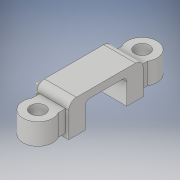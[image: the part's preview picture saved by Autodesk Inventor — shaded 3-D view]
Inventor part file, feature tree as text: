
AUTODESK INVENTOR PART (.ipt)
format: ipt  version: 2018 (Build 220112000, 112)  size: 198,144 bytes
history: native  units: in
note: dims shown in document units (in); Inventor stores cm internally (conversion verified against a paired STEP export)
features: sketch x10, extrude x6, fillet x2
ambient origin geometry x8: Origin, YZ Plane, XZ Plane, XY Plane, X Axis, Y Axis, Z Axis, Center Point
bodies: Solid1 (feature_tree)
feature tree (18):
  sketch  "Sketch1"  dims[d0=1.378in d1=0.5906in]
  sketch  "Sketch2"  dims[d2=0.1378in d3=0.0in d4=0.2559in d5=0.2559in]
  extrude  "Extrusion1"  Depth=0.5906in
  sketch  "Sketch4"  dims[d14=0.5512in d15=0.5512in]
  extrude  "Extrusion2"  Depth=0.1378in
  fillet  "Fillet2"  Radius=0.2559in
  sketch  "Sketch7"  dims[d18=0.4724in d19=0.0in d20=0.4724in d21=0.0in d22=0.0787in d23=0.0in]
  extrude  "Extrusion4"  Depth=0.1412in
  extrude  "Extrusion5"  Depth=0.5512in
  extrude  "Extrusion6"  Depth=0.2756in
  extrude  "Extrusion7"  Depth=0.4724in TaperAngle=0.0deg
  fillet  "Fillet4"  Radius=0.0787in
  sketch  "Sketch3"  dims[d6=0.4724in d7=0.0in d12=0.1412in]
  sketch  "Sketch5"  dims[d16=0.2756in d17=0.2756in]
  sketch  "Sketch8"  dims[d24=0.0472in]
  sketch  "Sketch9"  dims[d25=0.0472in]
  sketch  "Sketch10"  dims[d26=0.4724in d27=0.0in]
  sketch  "Sketch11"  dims[d28=0.0787in]
